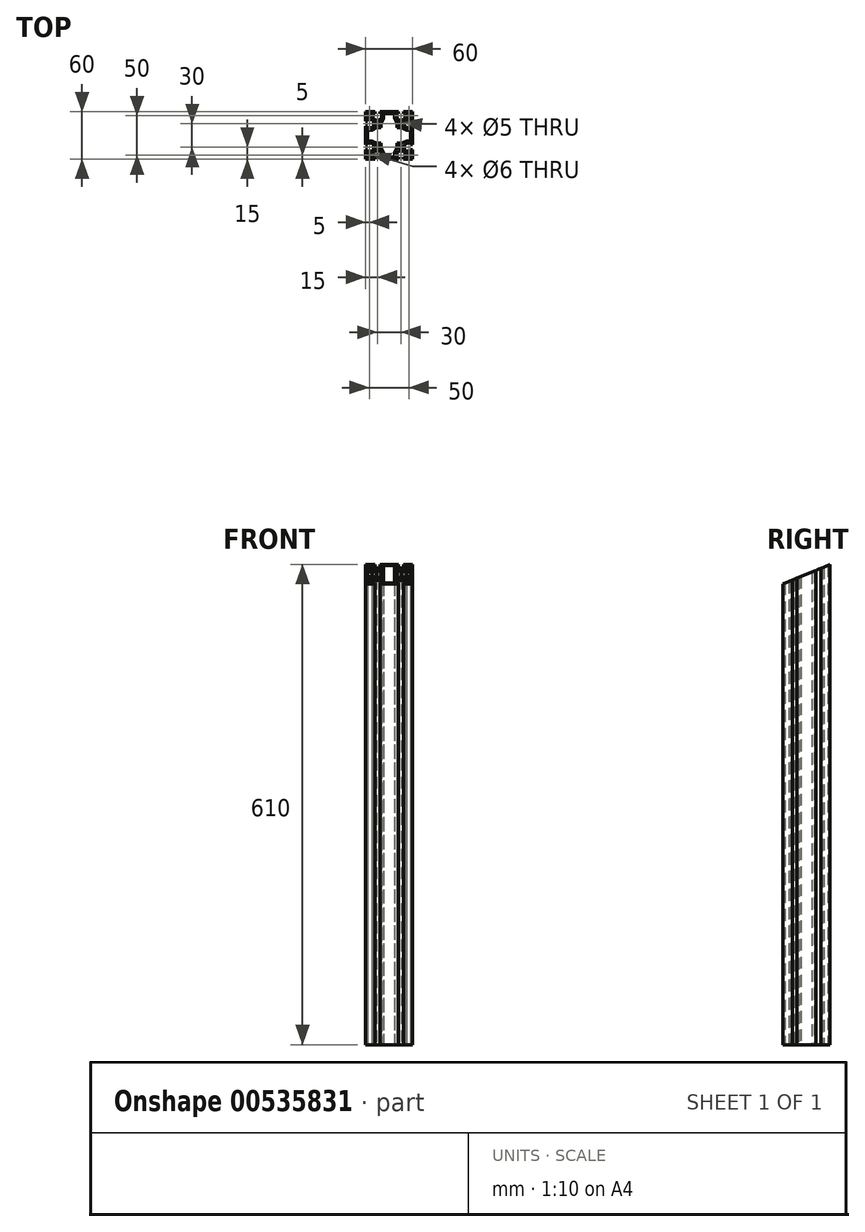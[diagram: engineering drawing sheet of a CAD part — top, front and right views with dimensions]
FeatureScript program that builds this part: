
annotation { "Feature Type Name" : "Feature", "Feature Type Description" : "" }
export const myFeature = defineFeature(function(context is Context, id is Id, definition is map)
    precondition{}
    {
        {
            var Q0;
            Q0=qCreatedBy(makeId("Top.planeOp"),FACE);
            var sketch = newSketch(context, id + "F0", { "sketchPlane" : qUnion([Q0])});
            skLineSegment(sketch, "E0.bottom", {"start": v(30, -30) * mm, "end": v(-30, -30) * mm});
            skLineSegment(sketch, "E0.top", {"start": v(30, 30) * mm, "end": v(-30, 30) * mm});
            skLineSegment(sketch, "E0.left", {"start": v(30, -30) * mm, "end": v(30, 30) * mm});
            skLineSegment(sketch, "E0.right", {"start": v(-30, -30) * mm, "end": v(-30, 30) * mm});
            skPoint(sketch, "E0.middle", {"position": v(0, 0) * mm});
            skLineSegment(sketch, "E1.top", {"start": v(-11.85, 30) * mm, "end": v(-18.15, 30) * mm});
            skLineSegment(sketch, "E1.left", {"start": v(-11.85, 27.5) * mm, "end": v(-11.85, 30) * mm});
            skLineSegment(sketch, "E1.right", {"start": v(-18.15, 27.5) * mm, "end": v(-18.15, 30) * mm});
            skPoint(sketch, "E1.middle", {"position": v(-15, 28.75) * mm});
            skLineSegment(sketch, "E2.bottom", {"start": v(-9.85, 27.5) * mm, "end": v(-11.85, 27.5) * mm});
            skLineSegment(sketch, "E2.left", {"start": v(-9.85, 27.5) * mm, "end": v(-9.85, 21.55) * mm});
            skLineSegment(sketch, "E2.right", {"start": v(-20.15, 27.5) * mm, "end": v(-20.15, 21.55) * mm});
            skPoint(sketch, "E2.middle", {"position": v(-15, 24.52) * mm});
            skArc(sketch, "E3", {"start": v(-20.15, 21.55) * mm, "mid": v(-15, 19.5) * mm, "end": v(-9.85, 21.55) * mm});
            skPoint(sketch, "E4.MirrorP", {"position": v(15, 24.52) * mm});
            skPoint(sketch, "E5.MirrorP", {"position": v(15, 28.75) * mm});
            skLineSegment(sketch, "E6.MirrorCS", {"start": v(11.85, 27.5) * mm, "end": v(11.85, 30) * mm});
            skLineSegment(sketch, "E7.MirrorCS", {"start": v(18.15, 27.5) * mm, "end": v(18.15, 30) * mm});
            skLineSegment(sketch, "E8.MirrorCS", {"start": v(9.85, 27.5) * mm, "end": v(11.85, 27.5) * mm});
            skLineSegment(sketch, "E9.MirrorCS", {"start": v(9.85, 27.5) * mm, "end": v(9.85, 21.55) * mm});
            skArc(sketch, "E10.MirrorCS", {"start": v(20.15, 21.55) * mm, "mid": v(15, 19.5) * mm, "end": v(9.85, 21.55) * mm});
            skLineSegment(sketch, "E11.MirrorCS", {"start": v(20.15, 27.5) * mm, "end": v(20.15, 21.55) * mm});
            skLineSegment(sketch, "E12.MirrorCS", {"start": v(11.85, 30) * mm, "end": v(18.15, 30) * mm});
            skLineSegment(sketch, "E13.1.0", {"start": v(27.5, 20.15) * mm, "end": v(21.55, 20.15) * mm});
            skLineSegment(sketch, "E13.1.1", {"start": v(27.5, 9.85) * mm, "end": v(21.55, 9.85) * mm});
            skArc(sketch, "E13.1.2", {"start": v(21.55, 20.15) * mm, "mid": v(19.5, 15) * mm, "end": v(21.55, 9.85) * mm});
            skLineSegment(sketch, "E13.1.3", {"start": v(27.5, -9.85) * mm, "end": v(21.55, -9.85) * mm});
            skLineSegment(sketch, "E13.1.4", {"start": v(27.5, -20.15) * mm, "end": v(21.55, -20.15) * mm});
            skPoint(sketch, "E13.1.5", {"position": v(28.75, 15) * mm});
            skPoint(sketch, "E13.1.6", {"position": v(28.75, -15) * mm});
            skArc(sketch, "E13.1.7", {"start": v(21.55, -20.15) * mm, "mid": v(19.5, -15) * mm, "end": v(21.55, -9.85) * mm});
            skPoint(sketch, "E13.1.8", {"position": v(24.52, -15) * mm});
            skPoint(sketch, "E13.1.9", {"position": v(24.52, 15) * mm});
            skLineSegment(sketch, "E13.1.10", {"start": v(27.5, 9.85) * mm, "end": v(27.5, 20.15) * mm});
            skLineSegment(sketch, "E13.1.11", {"start": v(27.5, -11.85) * mm, "end": v(27.5, -18.15) * mm});
            skLineSegment(sketch, "E13.1.12", {"start": v(30, 11.85) * mm, "end": v(30, 18.15) * mm});
            skLineSegment(sketch, "E13.1.13", {"start": v(30, -11.85) * mm, "end": v(30, -18.15) * mm});
            skLineSegment(sketch, "E13.1.14", {"start": v(27.5, 18.15) * mm, "end": v(30, 18.15) * mm});
            skLineSegment(sketch, "E13.1.15", {"start": v(27.5, 11.85) * mm, "end": v(30, 11.85) * mm});
            skLineSegment(sketch, "E13.1.16", {"start": v(27.5, 11.85) * mm, "end": v(27.5, 18.15) * mm});
            skLineSegment(sketch, "E13.1.17", {"start": v(27.5, -9.85) * mm, "end": v(27.5, -20.15) * mm});
            skLineSegment(sketch, "E13.1.18", {"start": v(27.5, -18.15) * mm, "end": v(30, -18.15) * mm});
            skLineSegment(sketch, "E13.1.19", {"start": v(27.5, -11.85) * mm, "end": v(30, -11.85) * mm});
            skLineSegment(sketch, "E13.2.0", {"start": v(20.15, -27.5) * mm, "end": v(20.15, -21.55) * mm});
            skLineSegment(sketch, "E13.2.1", {"start": v(9.85, -27.5) * mm, "end": v(9.85, -21.55) * mm});
            skArc(sketch, "E13.2.2", {"start": v(20.15, -21.55) * mm, "mid": v(15, -19.5) * mm, "end": v(9.85, -21.55) * mm});
            skLineSegment(sketch, "E13.2.3", {"start": v(-9.85, -27.5) * mm, "end": v(-9.85, -21.55) * mm});
            skLineSegment(sketch, "E13.2.4", {"start": v(-20.15, -27.5) * mm, "end": v(-20.15, -21.55) * mm});
            skPoint(sketch, "E13.2.5", {"position": v(15, -28.75) * mm});
            skPoint(sketch, "E13.2.6", {"position": v(-15, -28.75) * mm});
            skArc(sketch, "E13.2.7", {"start": v(-20.15, -21.55) * mm, "mid": v(-15, -19.5) * mm, "end": v(-9.85, -21.55) * mm});
            skPoint(sketch, "E13.2.8", {"position": v(-15, -24.52) * mm});
            skPoint(sketch, "E13.2.9", {"position": v(15, -24.52) * mm});
            skLineSegment(sketch, "E13.2.10", {"start": v(9.85, -27.5) * mm, "end": v(20.15, -27.5) * mm});
            skLineSegment(sketch, "E13.2.11", {"start": v(-11.85, -27.5) * mm, "end": v(-18.15, -27.5) * mm});
            skLineSegment(sketch, "E13.2.12", {"start": v(11.85, -30) * mm, "end": v(18.15, -30) * mm});
            skLineSegment(sketch, "E13.2.13", {"start": v(-11.85, -30) * mm, "end": v(-18.15, -30) * mm});
            skLineSegment(sketch, "E13.2.14", {"start": v(18.15, -27.5) * mm, "end": v(18.15, -30) * mm});
            skLineSegment(sketch, "E13.2.15", {"start": v(11.85, -27.5) * mm, "end": v(11.85, -30) * mm});
            skLineSegment(sketch, "E13.2.16", {"start": v(11.85, -27.5) * mm, "end": v(18.15, -27.5) * mm});
            skLineSegment(sketch, "E13.2.17", {"start": v(-9.85, -27.5) * mm, "end": v(-20.15, -27.5) * mm});
            skLineSegment(sketch, "E13.2.18", {"start": v(-18.15, -27.5) * mm, "end": v(-18.15, -30) * mm});
            skLineSegment(sketch, "E13.2.19", {"start": v(-11.85, -27.5) * mm, "end": v(-11.85, -30) * mm});
            skLineSegment(sketch, "E13.3.0", {"start": v(-27.5, -20.15) * mm, "end": v(-21.55, -20.15) * mm});
            skLineSegment(sketch, "E13.3.1", {"start": v(-27.5, -9.85) * mm, "end": v(-21.55, -9.85) * mm});
            skArc(sketch, "E13.3.2", {"start": v(-21.55, -20.15) * mm, "mid": v(-19.5, -15) * mm, "end": v(-21.55, -9.85) * mm});
            skLineSegment(sketch, "E13.3.3", {"start": v(-27.5, 9.85) * mm, "end": v(-21.55, 9.85) * mm});
            skLineSegment(sketch, "E13.3.4", {"start": v(-27.5, 20.15) * mm, "end": v(-21.55, 20.15) * mm});
            skPoint(sketch, "E13.3.5", {"position": v(-28.75, -15) * mm});
            skPoint(sketch, "E13.3.6", {"position": v(-28.75, 15) * mm});
            skArc(sketch, "E13.3.7", {"start": v(-21.55, 20.15) * mm, "mid": v(-19.5, 15) * mm, "end": v(-21.55, 9.85) * mm});
            skPoint(sketch, "E13.3.8", {"position": v(-24.52, 15) * mm});
            skPoint(sketch, "E13.3.9", {"position": v(-24.52, -15) * mm});
            skLineSegment(sketch, "E13.3.10", {"start": v(-27.5, -9.85) * mm, "end": v(-27.5, -20.15) * mm});
            skLineSegment(sketch, "E13.3.11", {"start": v(-27.5, 11.85) * mm, "end": v(-27.5, 18.15) * mm});
            skLineSegment(sketch, "E13.3.12", {"start": v(-30, -11.85) * mm, "end": v(-30, -18.15) * mm});
            skLineSegment(sketch, "E13.3.13", {"start": v(-30, 11.85) * mm, "end": v(-30, 18.15) * mm});
            skLineSegment(sketch, "E13.3.14", {"start": v(-27.5, -18.15) * mm, "end": v(-30, -18.15) * mm});
            skLineSegment(sketch, "E13.3.15", {"start": v(-27.5, -11.85) * mm, "end": v(-30, -11.85) * mm});
            skLineSegment(sketch, "E13.3.16", {"start": v(-27.5, -11.85) * mm, "end": v(-27.5, -18.15) * mm});
            skLineSegment(sketch, "E13.3.17", {"start": v(-27.5, 9.85) * mm, "end": v(-27.5, 20.15) * mm});
            skLineSegment(sketch, "E13.3.18", {"start": v(-27.5, 18.15) * mm, "end": v(-30, 18.15) * mm});
            skLineSegment(sketch, "E13.3.19", {"start": v(-27.5, 11.85) * mm, "end": v(-30, 11.85) * mm});
            skLineSegment(sketch, "E13.anchor1", {"start": v(0, 0) * mm, "end": v(-20.15, 21.55) * mm, "construction": true});
            skLineSegment(sketch, "E13.anchor2", {"start": v(0, 0) * mm, "end": v(-21.55, -20.15) * mm, "construction": true});
            skLineSegment(sketch, "E14.trimOffspring", {"start": v(-18.15, 27.5) * mm, "end": v(-20.15, 27.5) * mm});
            skLineSegment(sketch, "E15.trimOffspring", {"start": v(18.15, 27.5) * mm, "end": v(20.15, 27.5) * mm});
            skCircle(sketch, "E16", {"center": v(-15, 15) * mm, "radius": 2.5 * mm});
            skCircle(sketch, "E17", {"center": v(-25, 25) * mm, "radius": 3 * mm});
            skCircle(sketch, "E18.MirrorC", {"center": v(25, 25) * mm, "radius": 3 * mm});
            skCircle(sketch, "E19.MirrorC", {"center": v(25, -25) * mm, "radius": 3 * mm});
            skCircle(sketch, "E20.MirrorC", {"center": v(-25, -25) * mm, "radius": 3 * mm});
            skCircle(sketch, "E21.MirrorC", {"center": v(15, 15) * mm, "radius": 2.5 * mm});
            skCircle(sketch, "E22.MirrorC", {"center": v(15, -15) * mm, "radius": 2.5 * mm});
            skCircle(sketch, "E23.MirrorC", {"center": v(-15, -15) * mm, "radius": 2.5 * mm});
            skLineSegment(sketch, "E24", {"start": v(-7, 27.5) * mm, "end": v(0, 27.5) * mm});
            skLineSegment(sketch, "E25", {"start": v(-7, 27.5) * mm, "end": v(-7, 22) * mm});
            skLineSegment(sketch, "E26", {"start": v(-10, 10) * mm, "end": v(-10, 16) * mm});
            skLineSegment(sketch, "E27", {"start": v(-10, 16) * mm, "end": v(-7, 22) * mm});
            skLineSegment(sketch, "E28.MirrorCS", {"start": v(10, 10) * mm, "end": v(10, 16) * mm});
            skLineSegment(sketch, "E29.MirrorCS", {"start": v(10, 16) * mm, "end": v(7, 22) * mm});
            skLineSegment(sketch, "E30.MirrorCS", {"start": v(7, 27.5) * mm, "end": v(0, 27.5) * mm});
            skLineSegment(sketch, "E31.MirrorCS", {"start": v(7, 27.5) * mm, "end": v(7, 22) * mm});
            skLineSegment(sketch, "E32.1.0", {"start": v(-10, -10) * mm, "end": v(-16, -10) * mm});
            skLineSegment(sketch, "E32.1.1", {"start": v(-16, -10) * mm, "end": v(-22, -7) * mm});
            skLineSegment(sketch, "E32.1.2", {"start": v(-27.5, -7) * mm, "end": v(-22, -7) * mm});
            skLineSegment(sketch, "E32.1.3", {"start": v(-27.5, -7) * mm, "end": v(-27.5, 0) * mm});
            skLineSegment(sketch, "E32.1.4", {"start": v(-27.5, 7) * mm, "end": v(-27.5, 0) * mm});
            skLineSegment(sketch, "E32.1.5", {"start": v(-27.5, 7) * mm, "end": v(-22, 7) * mm});
            skLineSegment(sketch, "E32.1.6", {"start": v(-16, 10) * mm, "end": v(-22, 7) * mm});
            skLineSegment(sketch, "E32.1.7", {"start": v(-10, 10) * mm, "end": v(-16, 10) * mm});
            skLineSegment(sketch, "E32.2.0", {"start": v(10, -10) * mm, "end": v(10, -16) * mm});
            skLineSegment(sketch, "E32.2.1", {"start": v(10, -16) * mm, "end": v(7, -22) * mm});
            skLineSegment(sketch, "E32.2.2", {"start": v(7, -27.5) * mm, "end": v(7, -22) * mm});
            skLineSegment(sketch, "E32.2.3", {"start": v(7, -27.5) * mm, "end": v(0, -27.5) * mm});
            skLineSegment(sketch, "E32.2.4", {"start": v(-7, -27.5) * mm, "end": v(0, -27.5) * mm});
            skLineSegment(sketch, "E32.2.5", {"start": v(-7, -27.5) * mm, "end": v(-7, -22) * mm});
            skLineSegment(sketch, "E32.2.6", {"start": v(-10, -16) * mm, "end": v(-7, -22) * mm});
            skLineSegment(sketch, "E32.2.7", {"start": v(-10, -10) * mm, "end": v(-10, -16) * mm});
            skLineSegment(sketch, "E32.3.0", {"start": v(10, 10) * mm, "end": v(16, 10) * mm});
            skLineSegment(sketch, "E32.3.1", {"start": v(16, 10) * mm, "end": v(22, 7) * mm});
            skLineSegment(sketch, "E32.3.2", {"start": v(27.5, 7) * mm, "end": v(22, 7) * mm});
            skLineSegment(sketch, "E32.3.3", {"start": v(27.5, 7) * mm, "end": v(27.5, 0) * mm});
            skLineSegment(sketch, "E32.3.4", {"start": v(27.5, -7) * mm, "end": v(27.5, 0) * mm});
            skLineSegment(sketch, "E32.3.5", {"start": v(27.5, -7) * mm, "end": v(22, -7) * mm});
            skLineSegment(sketch, "E32.3.6", {"start": v(16, -10) * mm, "end": v(22, -7) * mm});
            skLineSegment(sketch, "E32.3.7", {"start": v(10, -10) * mm, "end": v(16, -10) * mm});
            skSolve(sketch);
        }
        {
            var Q0;
            {var subQ30=sQuery(id+"F0.wireOp",EDGE,"E1.left");Q0=makeQuery(id+"F0.imprint","IMPRINT",FACE,{"disambiguationData":[TD([[makeQuery(id+"F0.imprint","IMPRINT",EDGE,{"derivedFrom":subQ30}),-1.0]])]});}
            extrude(context, id + "F1", {"entities" : qUnion([Q0]), "depth" : 610 * mm, "offsetDistance" : 25 * mm});
        }
        {
            var Q0;
            Q0=makeQuery(id+"F1.opExtrude","SWEPT_EDGE",EDGE,{"disambiguationData":[OSD([sQuery(id+"F0.wireOp",EDGE,"E24"),sQuery(id+"F0.wireOp",EDGE,"E25")])]});
            var Q1;
            Q1=makeQuery(id+"F1.opExtrude","SWEPT_EDGE",EDGE,{"disambiguationData":[OSD([sQuery(id+"F0.wireOp",EDGE,"E30.MirrorCS"),sQuery(id+"F0.wireOp",EDGE,"E31.MirrorCS")])]});
            var Q2;
            Q2=makeQuery(id+"F1.opExtrude","SWEPT_EDGE",EDGE,{"disambiguationData":[OSD([sQuery(id+"F0.wireOp",EDGE,"840db5bc-c403-45cd-90c7-254e62d9e8c5.3.2"),sQuery(id+"F0.wireOp",EDGE,"840db5bc-c403-45cd-90c7-254e62d9e8c5.3.3")])]});
            var Q3;
            Q3=makeQuery(id+"F1.opExtrude","SWEPT_EDGE",EDGE,{"disambiguationData":[OSD([sQuery(id+"F0.wireOp",EDGE,"840db5bc-c403-45cd-90c7-254e62d9e8c5.3.4"),sQuery(id+"F0.wireOp",EDGE,"840db5bc-c403-45cd-90c7-254e62d9e8c5.3.5")])]});
            var Q4;
            Q4=makeQuery(id+"F1.opExtrude","SWEPT_EDGE",EDGE,{"disambiguationData":[OSD([sQuery(id+"F0.wireOp",EDGE,"840db5bc-c403-45cd-90c7-254e62d9e8c5.1.4"),sQuery(id+"F0.wireOp",EDGE,"840db5bc-c403-45cd-90c7-254e62d9e8c5.1.5")])]});
            var Q5;
            Q5=makeQuery(id+"F1.opExtrude","SWEPT_EDGE",EDGE,{"disambiguationData":[OSD([sQuery(id+"F0.wireOp",EDGE,"840db5bc-c403-45cd-90c7-254e62d9e8c5.1.2"),sQuery(id+"F0.wireOp",EDGE,"840db5bc-c403-45cd-90c7-254e62d9e8c5.1.3")])]});
            var Q6;
            Q6=makeQuery(id+"F1.opExtrude","SWEPT_EDGE",EDGE,{"disambiguationData":[OSD([sQuery(id+"F0.wireOp",EDGE,"840db5bc-c403-45cd-90c7-254e62d9e8c5.2.2"),sQuery(id+"F0.wireOp",EDGE,"840db5bc-c403-45cd-90c7-254e62d9e8c5.2.3")])]});
            var Q7;
            Q7=makeQuery(id+"F1.opExtrude","SWEPT_EDGE",EDGE,{"disambiguationData":[OSD([sQuery(id+"F0.wireOp",EDGE,"840db5bc-c403-45cd-90c7-254e62d9e8c5.2.4"),sQuery(id+"F0.wireOp",EDGE,"840db5bc-c403-45cd-90c7-254e62d9e8c5.2.5")])]});
            fillet(context, id + "F2", {"entities" : qUnion([Q0, Q1, Q2, Q3, Q4, Q5, Q6, Q7]), "radius" : 2 * mm, "tangentPropagation" : true, "allowEdgeOverflow" : false});
        }
        {
            var Q0;
            Q0=makeQuery(id+"F1.opExtrude","SWEPT_EDGE",EDGE,{"disambiguationData":[OSD([sQuery(id+"F0.wireOp",EDGE,"E26"),sQuery(id+"F0.wireOp",EDGE,"E27")])]});
            var Q1;
            Q1=makeQuery(id+"F1.opExtrude","SWEPT_EDGE",EDGE,{"disambiguationData":[OSD([sQuery(id+"F0.wireOp",EDGE,"E28.MirrorCS"),sQuery(id+"F0.wireOp",EDGE,"E29.MirrorCS")])]});
            var Q2;
            Q2=makeQuery(id+"F1.opExtrude","SWEPT_EDGE",EDGE,{"disambiguationData":[OSD([sQuery(id+"F0.wireOp",EDGE,"840db5bc-c403-45cd-90c7-254e62d9e8c5.3.0"),sQuery(id+"F0.wireOp",EDGE,"840db5bc-c403-45cd-90c7-254e62d9e8c5.3.1")])]});
            var Q3;
            Q3=makeQuery(id+"F1.opExtrude","SWEPT_EDGE",EDGE,{"disambiguationData":[OSD([sQuery(id+"F0.wireOp",EDGE,"840db5bc-c403-45cd-90c7-254e62d9e8c5.1.6"),sQuery(id+"F0.wireOp",EDGE,"840db5bc-c403-45cd-90c7-254e62d9e8c5.1.7")])]});
            var Q4;
            Q4=makeQuery(id+"F1.opExtrude","SWEPT_EDGE",EDGE,{"disambiguationData":[OSD([sQuery(id+"F0.wireOp",EDGE,"840db5bc-c403-45cd-90c7-254e62d9e8c5.1.0"),sQuery(id+"F0.wireOp",EDGE,"840db5bc-c403-45cd-90c7-254e62d9e8c5.1.1")])]});
            var Q5;
            Q5=makeQuery(id+"F1.opExtrude","SWEPT_EDGE",EDGE,{"disambiguationData":[OSD([sQuery(id+"F0.wireOp",EDGE,"840db5bc-c403-45cd-90c7-254e62d9e8c5.3.6"),sQuery(id+"F0.wireOp",EDGE,"840db5bc-c403-45cd-90c7-254e62d9e8c5.3.7")])]});
            var Q6;
            Q6=makeQuery(id+"F1.opExtrude","SWEPT_EDGE",EDGE,{"disambiguationData":[OSD([sQuery(id+"F0.wireOp",EDGE,"840db5bc-c403-45cd-90c7-254e62d9e8c5.2.0"),sQuery(id+"F0.wireOp",EDGE,"840db5bc-c403-45cd-90c7-254e62d9e8c5.2.1")])]});
            var Q7;
            Q7=makeQuery(id+"F1.opExtrude","SWEPT_EDGE",EDGE,{"disambiguationData":[OSD([sQuery(id+"F0.wireOp",EDGE,"840db5bc-c403-45cd-90c7-254e62d9e8c5.2.6"),sQuery(id+"F0.wireOp",EDGE,"840db5bc-c403-45cd-90c7-254e62d9e8c5.2.7")])]});
            fillet(context, id + "F3", {"entities" : qUnion([Q0, Q1, Q2, Q3, Q4, Q5, Q6, Q7]), "radius" : 7 * mm, "tangentPropagation" : true, "allowEdgeOverflow" : false});
        }
        {
            var Q0;
            Q0=qCreatedBy(makeId("Right.planeOp"),FACE);
            var sketch = newSketch(context, id + "F4", { "sketchPlane" : qUnion([Q0])});
            skLineSegment(sketch, "E33.bottom", {"start": v(-249.6, 768.34) * mm, "end": v(-66.93, 844) * mm});
            skLineSegment(sketch, "E33.top", {"start": v(-152.68, 534.33) * mm, "end": v(30, 610) * mm});
            skLineSegment(sketch, "E33.left", {"start": v(-249.6, 768.34) * mm, "end": v(-152.68, 534.33) * mm});
            skLineSegment(sketch, "E33.right", {"start": v(-66.93, 844) * mm, "end": v(30, 610) * mm});
            skSolve(sketch);
        }
        {
            var Q0;
            Q0 = qSketchRegion(id + "F4", true);
            extrude(context, id + "F5", {"entities" : qUnion([Q0]), "operationType" : NewBodyOperationType.REMOVE, "depth" : 30 * mm, "offsetDistance" : 25 * mm, "hasSecondDirection" : true, "secondDirectionOppositeDirection" : true, "secondDirectionDepth" : 30 * mm});
        }
    });
